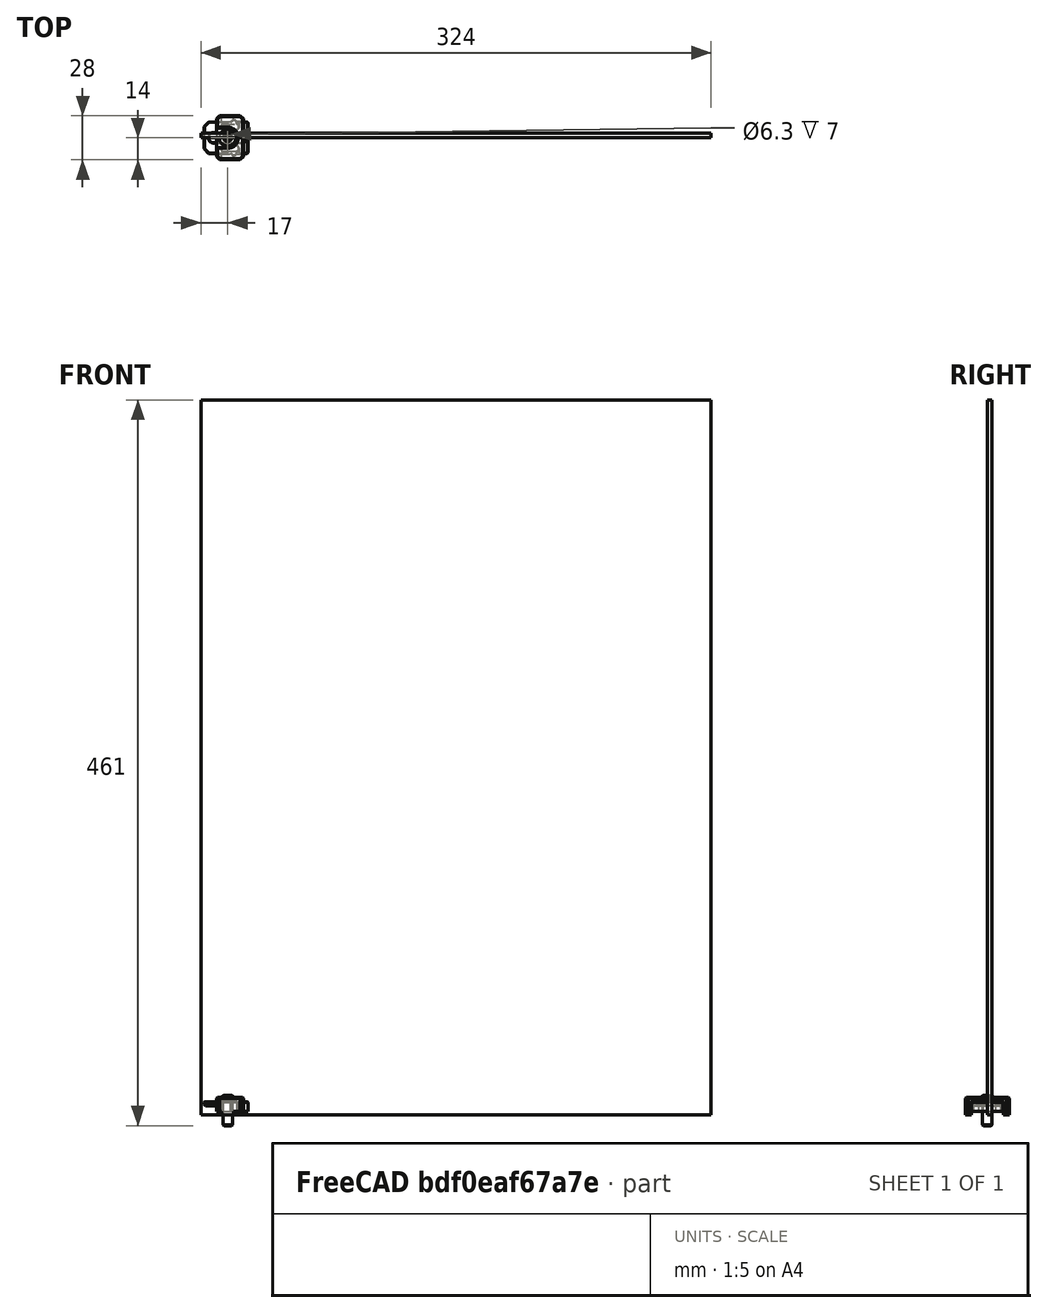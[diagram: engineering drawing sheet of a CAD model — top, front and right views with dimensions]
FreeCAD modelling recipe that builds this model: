
FCSTD DOCUMENT  (FreeCAD 0.19R24291 (Git))
Label: left-panel-assembly
License: All rights reserved
LicenseURL: http://en.wikipedia.org/wiki/All_rights_reserved
objects: Part::Feature×20, App::Part×11, Part::FeaturePython×10, Part::Box×1, PartDesign::CoordinateSystem×1
note: 32 computed .brp shape members not serialized (recipe doc carries the construction recipe); baked Part::Feature solids carry a one-line shape summary decoded from their .brp

FEATURE [Part::Feature] Chamfer008002001036  label="mounter-outer014"
  shape: bbox 17 x 28 x 11 mm, 53 faces (baked)
FEATURE [Part::Box] Box003  label="panel-324x454x3mm001"
  AttacherType = Attacher::AttachEngine3D
  Height = 454
  Length = 324
  Placement = pos=(-2,0,-2) rot=(0,0,1;0rad)
  Width = 3
FEATURE [Part::Feature] Chamfer008002001027  label="mounter-outer019"
  shape: bbox 17 x 28 x 11 mm, 53 faces (baked)
FEATURE [Part::Feature] Chamfer008002001037  label="mounter-inner018"
  shape: bbox 28 x 22 x 6 mm, 82 faces (baked)
FEATURE [Part::FeaturePython] Screw075  label="M6x16-Screw025"  # Fasteners workbench fastener (typed FeaturePython)
  Placement = pos=(15,0,7) rot=(0,0,1;0rad)
  baseObject = -> Chamfer008002001043 [Edge135]
  diameter = 4
  invert = false
  length = 3
  lengthCustom = 16
  matchOuter = false
  offset = 0
  thread = false
  type = 40
FEATURE [Part::Feature] Chamfer008002001045
  shape: bbox 28 x 22 x 6 mm, 82 faces (baked)
FEATURE [Part::Feature] Chamfer008002001042  label="mounter-inner020"
  shape: bbox 28 x 22 x 6 mm, 82 faces (baked)
FEATURE [Part::FeaturePython] Screw073  label="M6x16-Screw023"  # Fasteners workbench fastener (typed FeaturePython)
  Placement = pos=(15,0,7) rot=(0,0,1;0rad)
  baseObject = -> Chamfer008002001039 [Edge135]
  diameter = 4
  invert = false
  length = 3
  lengthCustom = 16
  matchOuter = false
  offset = 0
  thread = false
  type = 40
FEATURE [Part::Feature] Chamfer008002001044
  shape: bbox 17 x 28 x 11 mm, 53 faces (baked)
FEATURE [Part::Feature] Chamfer008002001031  label="mounter-outer017"
  shape: bbox 17 x 28 x 11 mm, 53 faces (baked)
FEATURE [Part::FeaturePython] Screw067  label="M6x16-Screw017"  # Fasteners workbench fastener (typed FeaturePython)
  Placement = pos=(15,0,7) rot=(0,0,1;0rad)
  baseObject = -> Chamfer008002001027 [Edge135]
  diameter = 4
  invert = false
  length = 3
  lengthCustom = 16
  matchOuter = false
  offset = 0
  thread = false
  type = 40
FEATURE [PartDesign::CoordinateSystem] LCS_left_panel  label="LCS_left-panel"
  AttacherType = Attacher::AttachEngine3D
FEATURE [Part::FeaturePython] Screw076  label="M6x16-Screw026"  # Fasteners workbench fastener (typed FeaturePython)
  Placement = pos=(15,0,7) rot=(0,0,1;0rad)
  baseObject = -> Chamfer008002001044 [Edge135]
  diameter = 4
  invert = false
  length = 3
  lengthCustom = 16
  matchOuter = false
  offset = 0
  thread = false
  type = 40
FEATURE [App::Part] Part036  label="Panel-mounterr2-022"
  Group = -> [Chamfer008002001045,Chamfer008002001044,Screw076]
  Origin = -> Origin036
  Placement = pos=(5,3,215) rot=(0,0.707107,-0.707107;3.14159rad)
FEATURE [Part::FeaturePython] Screw072  label="M6x16-Screw022"  # Fasteners workbench fastener (typed FeaturePython)
  Placement = pos=(15,0,7) rot=(0,0,1;0rad)
  baseObject = -> Chamfer008002001036 [Edge135]
  diameter = 4
  invert = false
  length = 3
  lengthCustom = 16
  matchOuter = false
  offset = 0
  thread = false
  type = 40
FEATURE [Part::Feature] Chamfer008002001030  label="mounter-inner015"
  shape: bbox 28 x 22 x 6 mm, 82 faces (baked)
FEATURE [Part::FeaturePython] Screw068  label="M6x16-Screw018"  # Fasteners workbench fastener (typed FeaturePython)
  Placement = pos=(15,0,7) rot=(0,0,1;0rad)
  baseObject = -> Chamfer008002001029 [Edge135]
  diameter = 4
  invert = false
  length = 3
  lengthCustom = 16
  matchOuter = false
  offset = 0
  thread = false
  type = 40
FEATURE [App::Part] Part032  label="Panel-mounterr2-018"
  Group = -> [Chamfer008002001037,Chamfer008002001036,Screw072]
  Origin = -> Origin032
  Placement = pos=(281,3,445) rot=(-0.57735,0.57735,-0.57735;4.18879rad)
FEATURE [Part::Feature] Chamfer008002001033  label="mounter-inner016"
  shape: bbox 28 x 22 x 6 mm, 82 faces (baked)
FEATURE [Part::Feature] Chamfer008002001038  label="mounter-inner019"
  shape: bbox 28 x 22 x 6 mm, 82 faces (baked)
FEATURE [Part::FeaturePython] Screw069  label="M6x16-Screw019"  # Fasteners workbench fastener (typed FeaturePython)
  Placement = pos=(15,0,7) rot=(0,0,1;0rad)
  baseObject = -> Chamfer008002001031 [Edge135]
  diameter = 4
  invert = false
  length = 3
  lengthCustom = 16
  matchOuter = false
  offset = 0
  thread = false
  type = 40
FEATURE [App::Part] Part029  label="Panel-mounterr2-015"
  Group = -> [Chamfer008002001030,Chamfer008002001031,Screw069]
  Origin = -> Origin029
  Placement = pos=(315,3,39) rot=(-1,0,0;4.71239rad)
FEATURE [Part::FeaturePython] Screw066  label="M6x16-Screw016"  # Fasteners workbench fastener (typed FeaturePython)
  Placement = pos=(15,0,7) rot=(0,0,1;0rad)
  baseObject = -> Chamfer008002001025 [Edge135]
  diameter = 4
  invert = false
  length = 3
  lengthCustom = 16
  matchOuter = false
  offset = 0
  thread = false
  type = 40
FEATURE [Part::Feature] Chamfer008002001028  label="mounter-inner014"
  shape: bbox 28 x 22 x 6 mm, 82 faces (baked)
FEATURE [Part::Feature] Chamfer008002001034  label="mounter-outer015"
  shape: bbox 17 x 28 x 11 mm, 53 faces (baked)
FEATURE [Part::Feature] Chamfer008002001032  label="mounter-outer016"
  shape: bbox 17 x 28 x 11 mm, 53 faces (baked)
FEATURE [Part::FeaturePython] Screw070  label="M6x16-Screw020"  # Fasteners workbench fastener (typed FeaturePython)
  Placement = pos=(15,0,7) rot=(0,0,1;0rad)
  baseObject = -> Chamfer008002001032 [Edge135]
  diameter = 4
  invert = false
  length = 3
  lengthCustom = 16
  matchOuter = false
  offset = 0
  thread = false
  type = 40
FEATURE [App::Part] Part030  label="Panel-mounterr2-016"
  Group = -> [Chamfer008002001033,Chamfer008002001032,Screw070]
  Origin = -> Origin030
  Placement = pos=(315,3,215) rot=(-1,0,0;4.71239rad)
FEATURE [Part::Feature] Chamfer008002001029  label="mounter-outer018"
  shape: bbox 17 x 28 x 11 mm, 53 faces (baked)
FEATURE [App::Part] Part028  label="Panel-mounterr2-014"
  Group = -> [Chamfer008002001028,Chamfer008002001029,Screw068]
  Origin = -> Origin028
  Placement = pos=(280.5,3,5) rot=(-0.57735,-0.57735,0.57735;4.18879rad)
FEATURE [Part::Feature] Chamfer008002001043  label="mounter-outer012"
  shape: bbox 17 x 28 x 11 mm, 53 faces (baked)
FEATURE [App::Part] Part035  label="Panel-mounterr2-021"
  Group = -> [Chamfer008002001042,Chamfer008002001043,Screw075]
  Origin = -> Origin035
  Placement = pos=(39,3,445) rot=(-0.57735,0.57735,-0.57735;4.18879rad)
FEATURE [Part::FeaturePython] Screw071  label="M6x16-Screw021"  # Fasteners workbench fastener (typed FeaturePython)
  Placement = pos=(15,0,7) rot=(0,0,1;0rad)
  baseObject = -> Chamfer008002001034 [Edge135]
  diameter = 4
  invert = false
  length = 3
  lengthCustom = 16
  matchOuter = false
  offset = 0
  thread = false
  type = 40
FEATURE [Part::Feature] Chamfer008002001024  label="mounter-inner012"
  shape: bbox 28 x 22 x 6 mm, 82 faces (baked)
FEATURE [Part::Feature] Chamfer008002001025  label="mounter-outer020"
  shape: bbox 17 x 28 x 11 mm, 53 faces (baked)
FEATURE [App::Part] Part026  label="Panel-mounterr2-012"
  Group = -> [Chamfer008002001024,Chamfer008002001025,Screw066]
  Origin = -> Origin026
  Placement = pos=(39,3,5) rot=(-0.57735,-0.57735,0.57735;4.18879rad)
FEATURE [Part::Feature] Chamfer008002001026  label="mounter-inner013"
  shape: bbox 28 x 22 x 6 mm, 82 faces (baked)
FEATURE [App::Part] Part027  label="Panel-mounterr2-013"
  Group = -> [Chamfer008002001026,Chamfer008002001027,Screw067]
  Origin = -> Origin027
  Placement = pos=(160,3,5) rot=(-0.57735,-0.57735,0.57735;4.18879rad)
FEATURE [Part::Feature] Chamfer008002001039  label="mounter-outer013"
  shape: bbox 17 x 28 x 11 mm, 53 faces (baked)
FEATURE [App::Part] Part033  label="Panel-mounterr2-019"
  Group = -> [Chamfer008002001038,Chamfer008002001039,Screw073]
  Origin = -> Origin033
  Placement = pos=(160,3,445) rot=(-0.57735,0.57735,-0.57735;4.18879rad)
FEATURE [Part::Feature] Chamfer008002001035  label="mounter-inner017"
  shape: bbox 28 x 22 x 6 mm, 82 faces (baked)
FEATURE [App::Part] Part031  label="Panel-mounterr2-017"
  Group = -> [Chamfer008002001035,Chamfer008002001034,Screw071]
  Origin = -> Origin031
  Placement = pos=(315,3,411) rot=(-1,0,0;4.71239rad)
FEATURE [App::Part] Part025  label="left-panel"
  Group = -> [Box003,Part026,Part027,Part028,Part029,Part030,Part031,Part032,Part033,Part035,Part036,LCS_left_panel]
  Origin = -> Origin025
